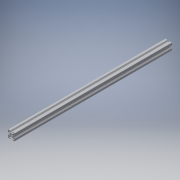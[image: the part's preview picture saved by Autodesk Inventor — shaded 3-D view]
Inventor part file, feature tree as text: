
AUTODESK INVENTOR PART (.ipt)
format: ipt  version: 2016 (Build 200138000, 138)  size: 404,480 bytes
history: native  units: in
note: dims shown in document units (in); Inventor stores cm internally (conversion verified against a paired STEP export)
features: other x3, sketch x2, extrude x1, hole x1, mirror x1
ambient origin geometry x8: Origin, YZ Plane, XZ Plane, XY Plane, X Axis, Y Axis, Z Axis, Center Point
bodies: Solid1 (feature_tree)
feature tree (8):
  other  "Blocks"
  extrude  "Extrusion1"  Depth=2.0in
  hole  "Hole1"  [1 undecoded]
  mirror  "Mirror1"
  sketch  "Sketch1"  dims[d1=0.0in d5=2.0in]
  other  "20x20"
  sketch  "Sketch3"  dims[d6=0.187in d7=0.75in d8=0.375in d9=0.25in d10=0.5635in d11=1.0in d12=0.8108in d13=1.0in d14=1.0in]
  other  "20x20:1"
note: 1 required parameter value undecoded (feature->parameter linkage not recoverable at this tier; creation-order binding heuristic only, values carry confidence <= 0.55)
